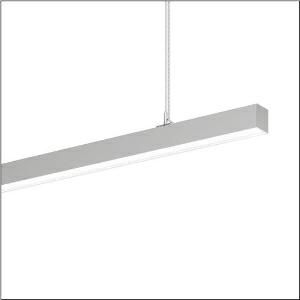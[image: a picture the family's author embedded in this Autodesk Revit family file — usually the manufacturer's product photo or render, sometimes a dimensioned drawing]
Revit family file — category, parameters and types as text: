
# Revit family: silica_r__21_51mx33db39sb_b1fc
name_source: partatom
category: Lighting Fixtures
units: mm (PartAtom-declared; Revit-internal decimal feet)

## family parameters
Cut with Voids When Loaded = No
Host = Face
Light Source = No
Part Type = Normal
Room Calculation Point = No
Round Connector Dimension = Use Diameter
Shared = No

## types (1)
- --- (1 x LED, 7390 lm, 51.6 W, 3000K)
    Apparent Load = 52 VA
    CIE Flux Codes = 78 96 99 55 100
    Color Rendering = 80
    Color Temperature = 3000K
    Default Elevation = 1800 mm
    Description = Silica® 21, office luminaire, primary optical cover: prismatic diffuser, of PMMA, CAT 2 (L<= 3000cd/m²), light emission: direct/indirect distribution, primary light characteristic: symmetric, installation type: suspended mounting, LED, rated luminous flux: 7.390lm, luminous efficacy: 143lm/W, light colour: 830, colour temperature: 3000K, with terminal, 3+2-pole, max. 2.5mm², mains connection: 220..240V, AC, 50/60Hz, rated input power: 51.6W, luminaire housing, of aluminium, metallic grey (RAL 9006), length: 1.504mm, width: 53mm, height: 53mm, protection rating (complete): IP20, insulation class (complete): insulation class I (protective earthing), certification: CE, permissible operating ambient temperature: 0..+35°C, standard: EN 50419, packaging unit: 1 piece
    Height = 53 mm
    Lamp = 1 x LED
    Lamp Light Flux = 7390 lm
    Lamp Power = 51.6 W
    Lamp count = 1
    Length = 1504 mm
    Luminous efficacy = 143 lm/W
    Manufacturer = Siteco
    ModVariant = No
    Model = 51MX33DB39SB
    Mounting Place = Ceiling
    Mounting Type = Pendant
    Number of Poles = 1
    OnlyDefault = Yes
    Power Factor = 1
    Product Name = Silica® 21
    Product group = office luminaire | ceiling pendant
    ProductGroupID = 902
    Protection Class = Protection class I
    Protection Degree = IP 20
    RLX_Detail_Level = 1
    RLX_Emergency_Light_Flux = 0 lm
    RLX_Emergency_Type = 0
    RLX_Emergency_Type_DB = No
    RlxData = <blob elided: 23445 chars, md5=3a0b3bac>
    Socket = socket
    Standby Power = 0 W
    System Light Flux = 7390 lm
    System Power = 52 W
    Type Comments = factory setting: luminous flux: 100 % | dim-lin: 254 | 345 mA
    Type Image = l_1313621.jpg
    URL = http://relux.com
    VarID = @adj_066811
    Voltage = 0 V
    Weight = 0.00 kg
    Width = 53 mm

## geometry (parser evidence)
native form markers: Blend x4, Sweep x13
no freeform markers — native parametric forms only
